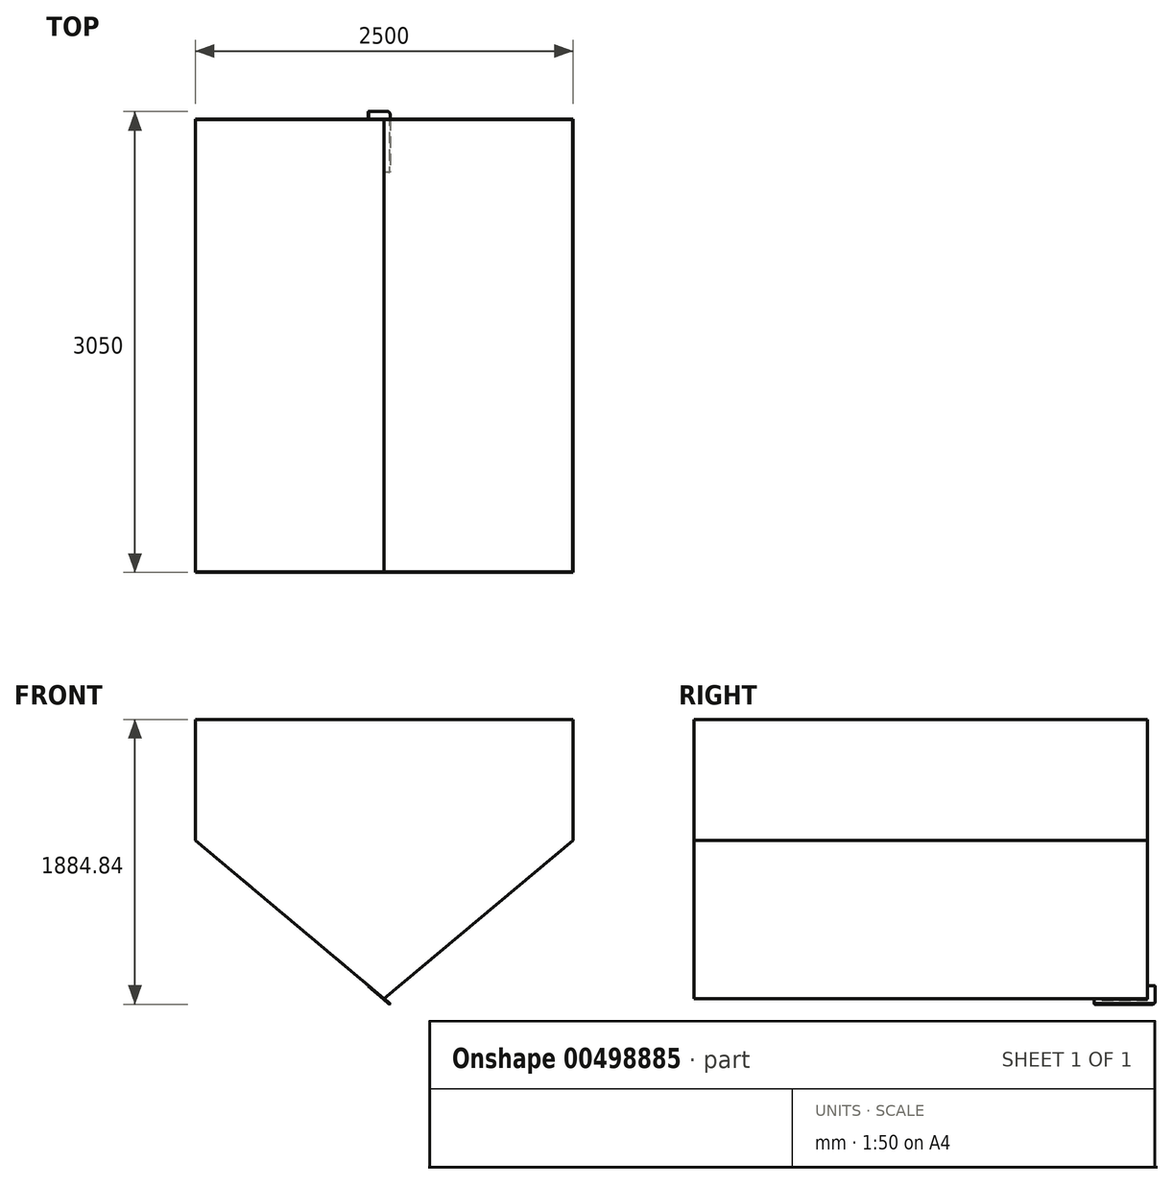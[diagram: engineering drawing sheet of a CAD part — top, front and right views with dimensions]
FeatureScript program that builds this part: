
annotation { "Feature Type Name" : "Feature", "Feature Type Description" : "" }
export const myFeature = defineFeature(function(context is Context, id is Id, definition is map)
    precondition{}
    {
        {
            var Q0;
            Q0=qCreatedBy(makeId("Front.planeOp"),FACE);
            var sketch = newSketch(context, id + "F0", { "sketchPlane" : qUnion([Q0])});
            skLineSegment(sketch, "E0", {"start": v(0, 0) * mm, "end": v(1250, 1048.87) * mm});
            skLineSegment(sketch, "E1", {"start": v(1250, 1048.87) * mm, "end": v(1250, 1848.87) * mm});
            skLineSegment(sketch, "E2", {"start": v(1250, 1848.87) * mm, "end": v(0, 1848.87) * mm});
            skLineSegment(sketch, "E3", {"start": v(0, 0) * mm, "end": v(0, 1266.69) * mm, "construction": true});
            skLineSegment(sketch, "E4.MirrorCS", {"start": v(0, 0) * mm, "end": v(-1250, 1048.87) * mm});
            skLineSegment(sketch, "E5.MirrorCS", {"start": v(-1250, 1048.87) * mm, "end": v(-1250, 1848.87) * mm});
            skLineSegment(sketch, "E6.MirrorCS", {"start": v(-1250, 1848.87) * mm, "end": v(0, 1848.87) * mm});
            skSolve(sketch);
        }
        {
            var Q0;
            Q0 = qSketchRegion(id + "F0", true);
            extrude(context, id + "F1", {"entities" : qUnion([Q0]), "depth" : 3000 * mm});
        }
        {
            var Q0;
            Q0=makeQuery(id+"F1.opExtrude","SWEPT_FACE",FACE,{"disambiguationData":[OSD([sQuery(id+"F0.wireOp",EDGE,"E2"),sQuery(id+"F0.wireOp",EDGE,"E6.MirrorCS")])]});
            shell(context, id + "F2", {"entities" : qUnion([Q0]), "thickness" : 2.5 * mm});
        }
        {
            var Q0;
            Q0=makeQuery(id+"F1.opExtrude","SWEPT_FACE",FACE,{"disambiguationData":[OSD([sQuery(id+"F0.wireOp",EDGE,"E4.MirrorCS")])]});
            var sketch = newSketch(context, id + "F3", { "sketchPlane" : qUnion([Q0])});
            skLineSegment(sketch, "E7", {"start": v(-135, 0) * mm, "end": v(-135, -45) * mm});
            skLineSegment(sketch, "E8", {"start": v(-130, -50) * mm, "end": v(30, -50) * mm});
            skLineSegment(sketch, "E9", {"start": v(50, -30) * mm, "end": v(50, 346) * mm});
            skLineSegment(sketch, "E10", {"start": v(45, 351) * mm, "end": v(0, 351) * mm});
            skLineSegment(sketch, "E11", {"start": v(0, 351) * mm, "end": v(0, 301) * mm});
            skLineSegment(sketch, "E12", {"start": v(0, 301) * mm, "end": v(6, 301) * mm});
            skLineSegment(sketch, "E13", {"start": v(6, 301) * mm, "end": v(6, 0) * mm});
            skLineSegment(sketch, "E14", {"start": v(6, 0) * mm, "end": v(-135, 0) * mm});
            skPoint(sketch, "E15.visualSharp", {"position": v(-135, -50) * mm});
            skArc(sketch, "E15.filletArc", {"start": v(-135, -45) * mm, "mid": v(-133.54, -48.54) * mm, "end": v(-130, -50) * mm});
            skPoint(sketch, "E16.visualSharp", {"position": v(50, -50) * mm});
            skArc(sketch, "E16.filletArc", {"start": v(30, -50) * mm, "mid": v(44.14, -44.14) * mm, "end": v(50, -30) * mm});
            skPoint(sketch, "E17.visualSharp", {"position": v(50, 351) * mm});
            skArc(sketch, "E17.filletArc", {"start": v(50, 346) * mm, "mid": v(48.54, 349.54) * mm, "end": v(45, 351) * mm});
            skSolve(sketch);
        }
        {
            var Q0;
            Q0 = qSketchRegion(id + "F3", true);
            extrude(context, id + "F4", {"entities" : qUnion([Q0]), "operationType" : NewBodyOperationType.ADD, "depth" : 5 * mm, "hasSecondDirection" : true, "secondDirectionOppositeDirection" : true, "secondDirectionDepth" : 1 * mm});
        }
    });
